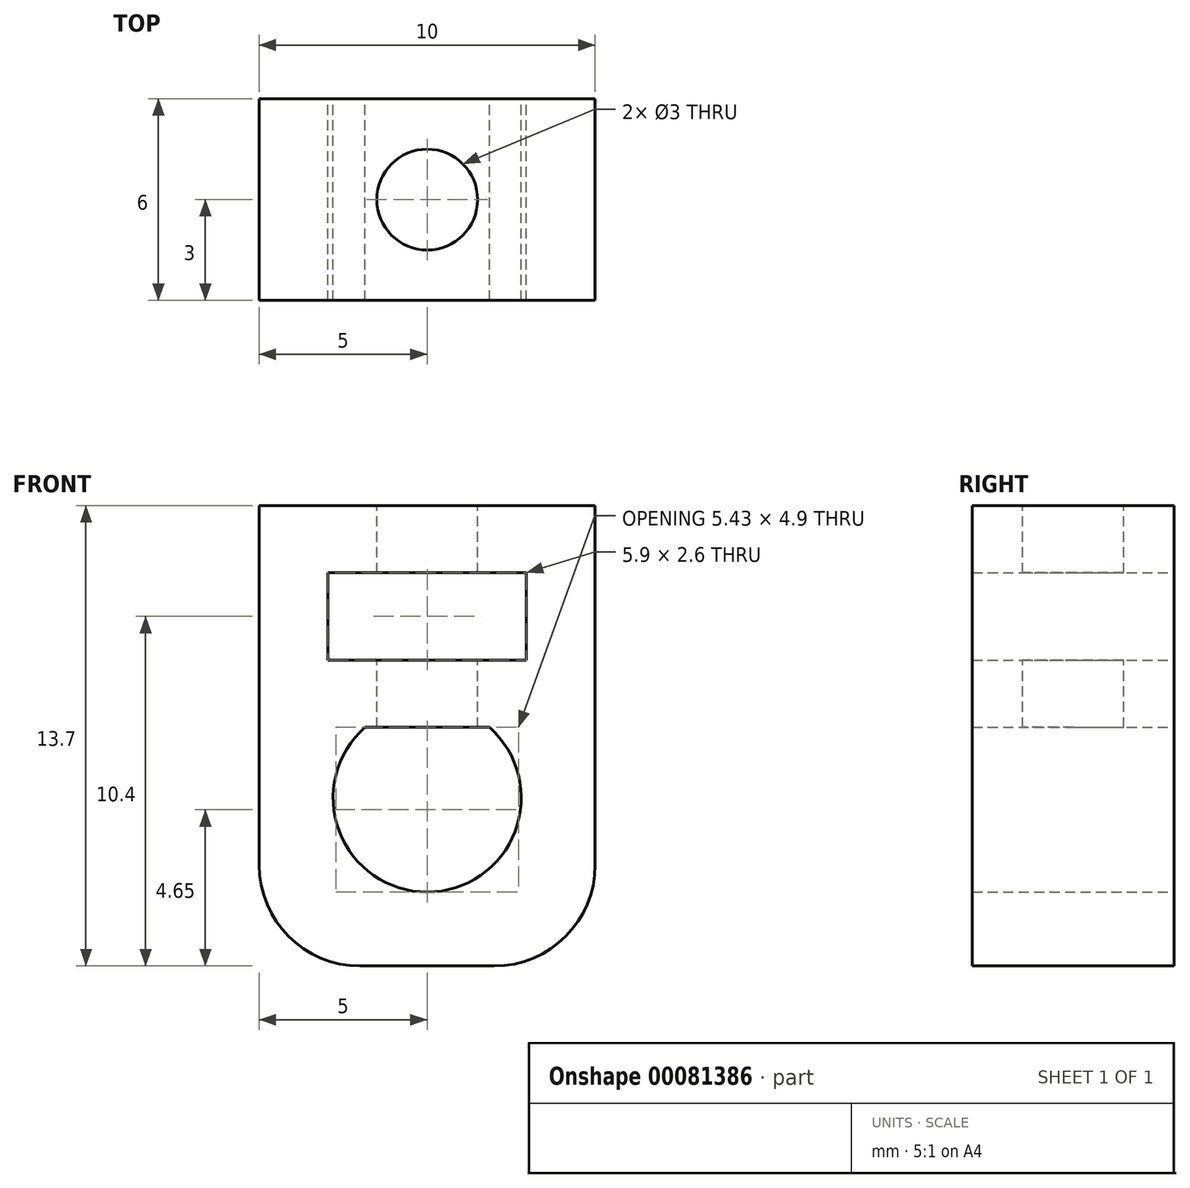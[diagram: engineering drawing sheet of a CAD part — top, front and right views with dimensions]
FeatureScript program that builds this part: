
annotation { "Feature Type Name" : "Feature", "Feature Type Description" : "" }
export const myFeature = defineFeature(function(context is Context, id is Id, definition is map)
    precondition{}
    {
        {
            var Q0;
            Q0=qCreatedBy(makeId("Front.planeOp"),FACE);
            var sketch = newSketch(context, id + "F0", { "sketchPlane" : qUnion([Q0])});
            skArc(sketch, "E0", {"start": v(-1.85, 2.1) * mm, "mid": v(0, -2.8) * mm, "end": v(1.85, 2.1) * mm});
            skLineSegment(sketch, "E1", {"start": v(0, 0) * mm, "end": v(0, 2.1) * mm, "construction": true});
            skLineSegment(sketch, "E2", {"start": v(0, 2.1) * mm, "end": v(-1.85, 2.1) * mm});
            skLineSegment(sketch, "E3.MirrorCS", {"start": v(0, 2.1) * mm, "end": v(1.85, 2.1) * mm});
            skLineSegment(sketch, "E4.bottom", {"start": v(5, -5) * mm, "end": v(-5, -5) * mm});
            skLineSegment(sketch, "E4.top", {"start": v(5, 5) * mm, "end": v(-5, 5) * mm, "construction": true});
            skLineSegment(sketch, "E4.left", {"start": v(5, -5) * mm, "end": v(5, 5) * mm});
            skLineSegment(sketch, "E4.right", {"start": v(-5, -5) * mm, "end": v(-5, 5) * mm});
            skLineSegment(sketch, "E5", {"start": v(-5, 5) * mm, "end": v(-5, 8.7) * mm});
            skLineSegment(sketch, "E6", {"start": v(-5, 8.7) * mm, "end": v(5, 8.7) * mm});
            skLineSegment(sketch, "E7", {"start": v(5, 8.7) * mm, "end": v(5, 5) * mm});
            skLineSegment(sketch, "E8.bottom", {"start": v(-2.95, 4.1) * mm, "end": v(2.95, 4.1) * mm});
            skLineSegment(sketch, "E8.top", {"start": v(-2.95, 6.7) * mm, "end": v(2.95, 6.7) * mm});
            skLineSegment(sketch, "E8.left", {"start": v(-2.95, 4.1) * mm, "end": v(-2.95, 6.7) * mm});
            skLineSegment(sketch, "E8.right", {"start": v(2.95, 4.1) * mm, "end": v(2.95, 6.7) * mm});
            skLineSegment(sketch, "E9", {"start": v(0, 4.1) * mm, "end": v(0, 2.1) * mm});
            skSolve(sketch);
        }
        {
            var Q0;
            Q0 = qSketchRegion(id + "F0", true);
            extrude(context, id + "F1", {"entities" : qUnion([Q0]), "depth" : 6 * mm});
        }
        {
            var Q0;
            Q0=makeQuery(id+"F1.opExtrude","SWEPT_FACE",FACE,{"disambiguationData":[OSD([sQuery(id+"F0.wireOp",EDGE,"E6")])]});
            var sketch = newSketch(context, id + "F2", { "sketchPlane" : qUnion([Q0])});
            skLineSegment(sketch, "E10.0.0", {"start": v(5, 0) * mm, "end": v(-5, 0) * mm, "construction": true});
            skLineSegment(sketch, "E10.0.1", {"start": v(-5, 0) * mm, "end": v(-5, -6) * mm, "construction": true});
            skLineSegment(sketch, "E10.0.2", {"start": v(-5, -6) * mm, "end": v(5, -6) * mm, "construction": true});
            skLineSegment(sketch, "E10.0.3", {"start": v(5, -6) * mm, "end": v(5, 0) * mm, "construction": true});
            skPoint(sketch, "E11", {"position": v(0, -3) * mm});
            skPoint(sketch, "E11.positionSnap0", {"position": v(-5, -3) * mm});
            skPoint(sketch, "E11.positionSnap1", {"position": v(0, 0) * mm});
            skCircle(sketch, "E12", {"center": v(0, -3) * mm, "radius": 1.5 * mm});
            skSolve(sketch);
        }
        {
            var Q0;
            Q0 = qSketchRegion(id + "F2", true);
            var Q1;
            Q1=makeQuery(id+"F1.opExtrude","SWEPT_FACE",FACE,{"disambiguationData":[OSD([sQuery(id+"F0.wireOp",EDGE,"E2"),sQuery(id+"F0.wireOp",EDGE,"E3.MirrorCS")])]});
            extrude(context, id + "F3", {"entities" : qUnion([Q0]), "operationType" : NewBodyOperationType.REMOVE, "endBound" : BoundingType.UP_TO_SURFACE, "oppositeDirection" : true, "endBoundEntityFace" : qUnion([Q1]), "depth" : 25 * mm});
        }
        {
            var Q0;
            Q0=makeQuery(id+"F1.opExtrude","SWEPT_EDGE",EDGE,{"disambiguationData":[OSD([sQuery(id+"F0.wireOp",EDGE,"E4.bottom"),sQuery(id+"F0.wireOp",EDGE,"E4.left")])]});
            var Q1;
            Q1=makeQuery(id+"F1.opExtrude","SWEPT_EDGE",EDGE,{"disambiguationData":[OSD([sQuery(id+"F0.wireOp",EDGE,"E4.bottom"),sQuery(id+"F0.wireOp",EDGE,"E4.right")])]});
            fillet(context, id + "F4", {"entities" : qUnion([Q0, Q1]), "radius" : 3 * mm, "tangentPropagation" : true, "allowEdgeOverflow" : false});
        }
    });
